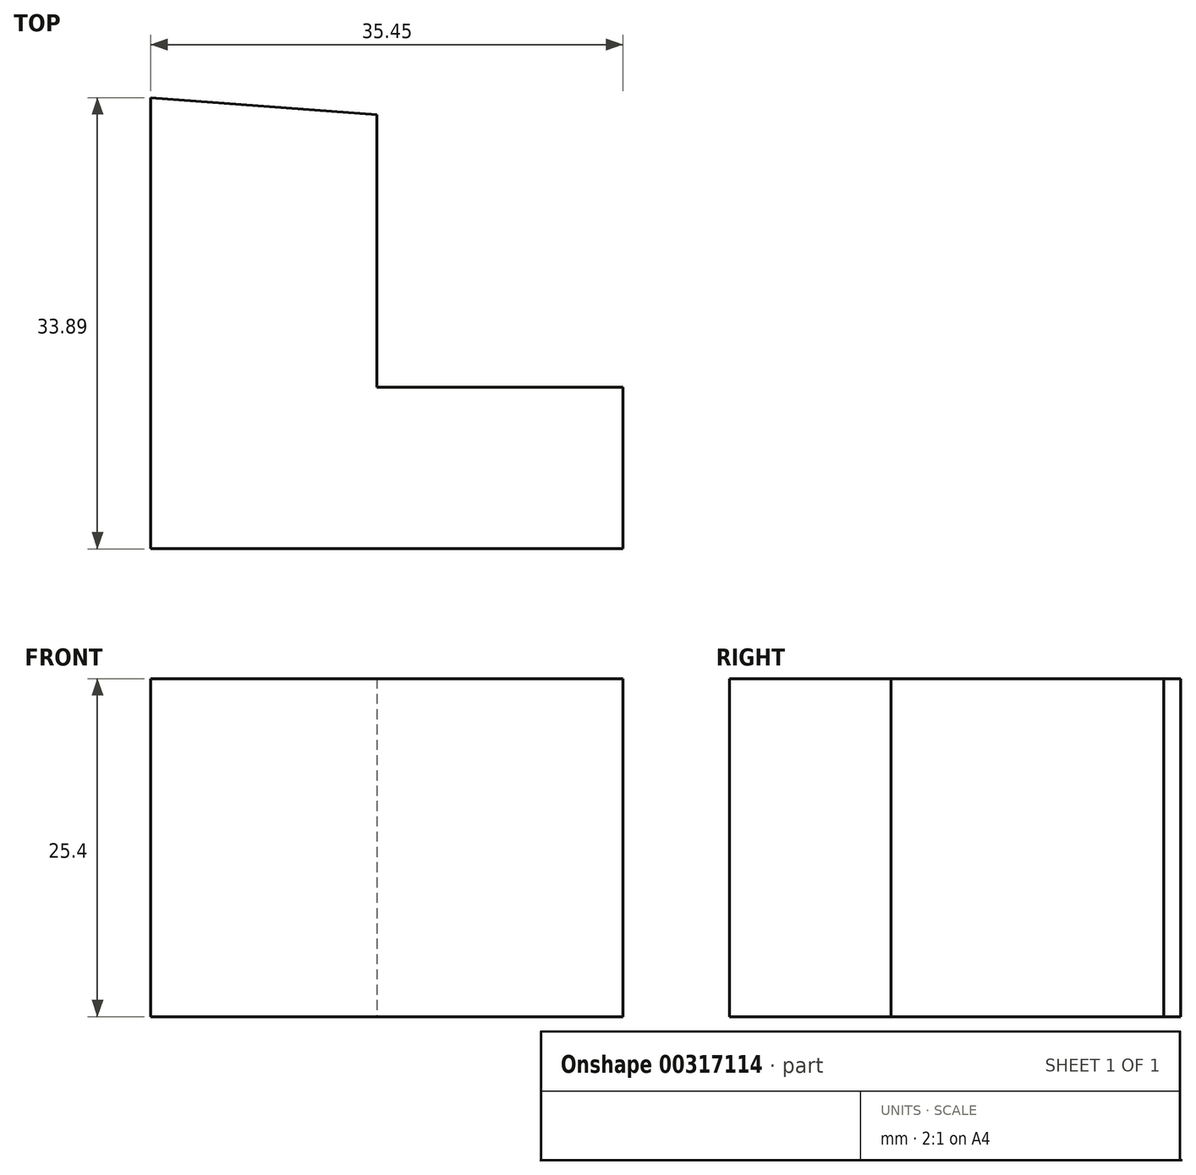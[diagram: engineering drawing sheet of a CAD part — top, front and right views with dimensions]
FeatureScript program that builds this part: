
annotation { "Feature Type Name" : "Feature", "Feature Type Description" : "" }
export const myFeature = defineFeature(function(context is Context, id is Id, definition is map)
    precondition{}
    {
        {
            var Q0;
            Q0=qCreatedBy(makeId("Top.planeOp"),FACE);
            var sketch = newSketch(context, id + "F0", { "sketchPlane" : qUnion([Q0])});
            skLineSegment(sketch, "E0", {"start": v(-28.56, 52.64) * mm, "end": v(-28.56, 18.75) * mm});
            skLineSegment(sketch, "E1", {"start": v(-28.56, 18.75) * mm, "end": v(6.89, 18.75) * mm});
            skLineSegment(sketch, "E2", {"start": v(6.89, 18.75) * mm, "end": v(6.89, 30.88) * mm});
            skLineSegment(sketch, "E3", {"start": v(6.89, 30.88) * mm, "end": v(-11.6, 30.88) * mm});
            skLineSegment(sketch, "E4", {"start": v(-11.6, 30.88) * mm, "end": v(-11.6, 51.37) * mm});
            skLineSegment(sketch, "E5", {"start": v(-11.6, 51.37) * mm, "end": v(-28.56, 52.64) * mm});
            skSolve(sketch);
        }
        {
            var Q0;
            Q0=makeQuery(id+"F0.imprint","IMPRINT",FACE,{"disambiguationData":[TD([[makeQuery(id+"F0.imprint","IMPRINT",EDGE,{"derivedFrom":sQuery(id+"F0.wireOp",EDGE,"E0")}),1.0]])]});
            extrude(context, id + "F1", {"entities" : qUnion([Q0]), "depth" : 25.4 * mm});
        }
    });
